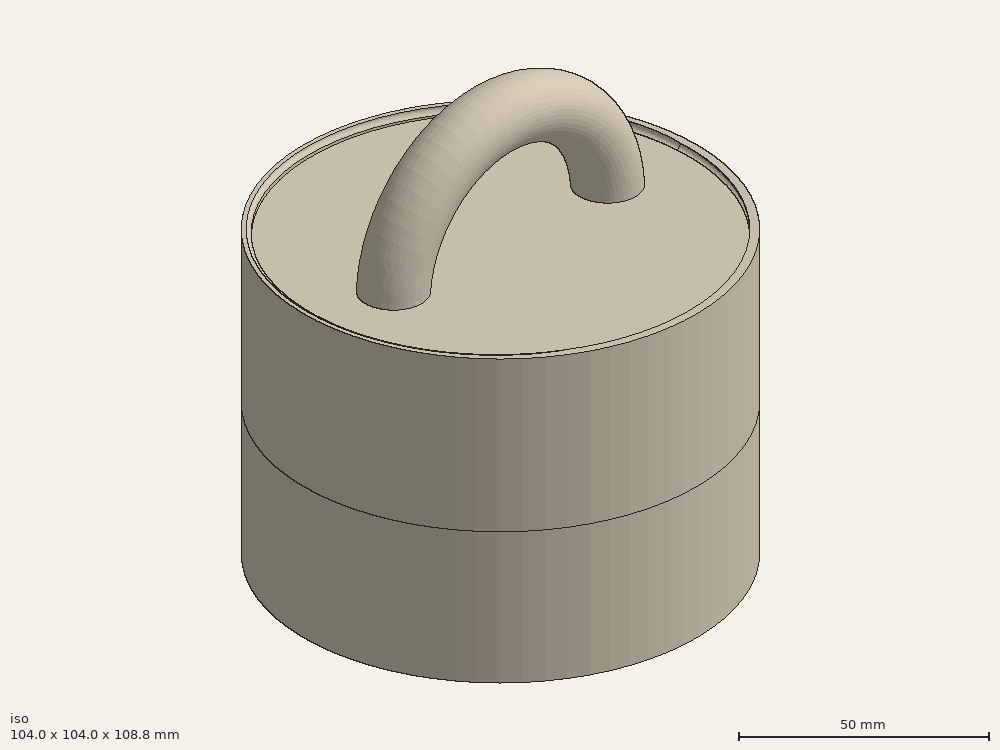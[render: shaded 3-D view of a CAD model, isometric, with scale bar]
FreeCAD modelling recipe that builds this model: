
FCSTD DOCUMENT  (FreeCAD 0.17R13522 (Git))
Label: tuna_wringer_all_3_parts
License: CreativeCommons Attribution-ShareAlike
LicenseURL: http://creativecommons.org/licenses/by-sa/4.0/
objects: Part::Cut×63, Part::Feature×46, Part::Cylinder×26, Part::MultiFuse×13, Part::Box×10, Sketcher::SketchObject×10, Part::Extrusion×9, Part::Sweep×6, PartDesign::Body×4, Part::Helix×4, Part::Ellipse×3, Part::FeaturePython×3, Part::MultiCommon×3, PartDesign::ShapeBinder×3, App::DocumentObjectGroup×3
note: 203 computed .brp shape members not serialized (recipe doc carries the construction recipe); baked Part::Feature solids carry a one-line shape summary decoded from their .brp

FEATURE [Part::Cylinder] Cylinder001  label="base_parte_inferior"
  Angle = 360
  AttacherType = Attacher::AttachEngine3D
  Height = 35
  Placement = pos=(0,0,-30) rot=(0,0,1;0rad)
  Radius = 52
FEATURE [Part::Feature] Fusion001  label="base_roscada_media_para_roscar_recipiente_inferior"
  shape: bbox 110.9 x 119.3 x 43.76 mm, 46 faces (baked)
FEATURE [Part::Cut] Cut
  Base = -> Cylinder001
  Tool = -> Fusion001
FEATURE [Part::Cylinder] Cylinder002  label="perforador_parte_inferior"
  Angle = 360
  AttacherType = Attacher::AttachEngine3D
  Height = 29
  Placement = pos=(0,0,-28) rot=(0,0,1;0rad)
  Radius = 49
FEATURE [Part::Feature] Fusion002  label="base_roscada_media001"
  shape: bbox 110.9 x 119.3 x 43.76 mm, 46 faces (baked)
FEATURE [Part::Cylinder] Cylinder003  label="Cylinder001"
  Angle = 360
  AttacherType = Attacher::AttachEngine3D
  Height = 40
  Placement = pos=(0,0,5) rot=(0,0,1;0rad)
  Radius = 52
FEATURE [Part::MultiFuse] Fusion003  label="parte_media_comienzo"
  Shapes = -> [Fusion002,Cylinder003]
FEATURE [Part::Feature] Fusion004  label="base_roscada_media002"
  Placement = pos=(0,0,8) rot=(0,0,1;0rad)
  shape: bbox 110.9 x 119.3 x 43.76 mm, 46 faces (baked)
FEATURE [Part::Cut] Cut002  label="parte_media_2"
  Base = -> Fusion003
  Tool = -> Fusion004
FEATURE [Part::Cylinder] Cylinder004  label="Cylinder002"
  Angle = 360
  AttacherType = Attacher::AttachEngine3D
  Height = 10
  Placement = pos=(0,0,-10) rot=(0,0,1;0rad)
  Radius = 60
FEATURE [Part::Cut] Cut003  label="parte_media_sin_perforar"
  Base = -> Cut002
  Tool = -> Cylinder004
FEATURE [Part::Feature] Fusion005  label="tapa_rosca"
  shape: bbox 110.9 x 119.3 x 43.76 mm, 46 faces (baked)
FEATURE [Part::Cylinder] Cylinder005  label="Cylinder003"
  Angle = 360
  AttacherType = Attacher::AttachEngine3D
  Height = 40
  Placement = pos=(0,0,4) rot=(0,0,1;0rad)
  Radius = 54
FEATURE [Part::Cut] Cut004
  Base = -> Fusion005
  Tool = -> Cylinder005
FEATURE [Part::Cylinder] Cylinder006  label="Cylinder004"
  Angle = 360
  AttacherType = Attacher::AttachEngine3D
  Height = 1
  Placement = pos=(0,0,4) rot=(0,0,1;0rad)
  Radius = 50
FEATURE [Part::MultiFuse] Fusion006
  Shapes = -> [Cut004,Cylinder006]
FEATURE [Part::Ellipse] Ellipse
  Angle0 = 0
  Angle1 = 360
  AttacherType = Attacher::AttachEngine3D
  MajorRadius = 5
  MinorRadius = 2.5
FEATURE [Part::Extrusion] Extrude
  Base = -> Ellipse
  Dir = (0,0,1)
  DirMode = 2
  FaceMakerClass = Part::FaceMakerBullseye
  LengthFwd = 20
  LengthRev = 0
  Solid = true
  Symmetric = false
FEATURE [Part::Extrusion] Extrude001
  Base = -> Ellipse
  Dir = (0,0,1)
  DirMode = 2
  FaceMakerClass = Part::FaceMakerBullseye
  LengthFwd = 20
  LengthRev = 0
  Solid = true
  Symmetric = false
FEATURE [Part::Extrusion] Extrude002
  Base = -> Ellipse
  Dir = (0,0,1)
  DirMode = 2
  FaceMakerClass = Part::FaceMakerBullseye
  LengthFwd = 20
  LengthRev = 0
  Solid = true
  Symmetric = false
FEATURE [Part::FeaturePython] Array  # Draft array (typed FeaturePython)
  Angle = 360
  ArrayType = 0
  Axis = (0,0,1)
  Base = -> Extrude
  Center = (0,0,0)
  Fuse = false
  IntervalAxis = (0,0,0)
  IntervalX = (14,0,0)
  IntervalY = (0,9,0)
  IntervalZ = (0,0,0)
  NumberPolar = 1
  NumberX = 30
  NumberY = 30
  NumberZ = 1
FEATURE [Part::Cylinder] Cylinder007  label="Cylinder005"
  Angle = 360
  AttacherType = Attacher::AttachEngine3D
  Height = 50
  Placement = pos=(77,135,-2) rot=(0,0,1;0rad)
  Radius = 48
FEATURE [Part::MultiCommon] Common
  Placement = pos=(39,-136,0) rot=(0,0,1;0rad)
  Shapes = -> [Array,Cylinder007]
FEATURE [Part::Box] Box  label="Cube"
  AttacherType = Attacher::AttachEngine3D
  Height = 60
  Length = 10
  Placement = pos=(92,40,-5) rot=(0,0,1;0rad)
  Width = 10
FEATURE [Part::Feature] Box001  label="Cube001"
  Placement = pos=(132,40,-5) rot=(0,0,1;0rad)
  shape: bbox 10 x 10 x 60 mm, 6 faces (baked)
FEATURE [Part::Feature] Box001001  label="Cube002"
  Placement = pos=(146,30,-5) rot=(0,0,1;0rad)
  shape: bbox 10 x 10 x 60 mm, 6 faces (baked)
FEATURE [Part::Feature] Box001001001  label="Cube003"
  Placement = pos=(77,30,-5) rot=(0,0,1;0rad)
  shape: bbox 10 x 10 x 60 mm, 6 faces (baked)
FEATURE [Part::Feature] Box001001001001  label="Cube004"
  Placement = pos=(77,-43,-5) rot=(0,0,1;0rad)
  shape: bbox 10 x 10 x 60 mm, 6 faces (baked)
FEATURE [Part::Feature] Box001001001001001  label="Cube005"
  Placement = pos=(146,-43,-5) rot=(0,0,1;0rad)
  shape: bbox 10 x 10 x 60 mm, 6 faces (baked)
FEATURE [Part::Feature] Box001001001001001001  label="Cube006"
  Placement = pos=(130,-52,-5) rot=(0,0,1;0rad)
  shape: bbox 10 x 10 x 60 mm, 6 faces (baked)
FEATURE [Part::Feature] Box001001001001001001001  label="Cube007"
  Placement = pos=(91,-52,-5) rot=(0,0,1;0rad)
  shape: bbox 10 x 10 x 60 mm, 6 faces (baked)
FEATURE [Part::Feature] Box001001001001001001002  label="Cube008"
  Placement = pos=(64,13,-5) rot=(0,0,1;0rad)
  shape: bbox 10 x 10 x 60 mm, 6 faces (baked)
FEATURE [Part::Feature] Box001001001001001001002001  label="Cube009"
  Placement = pos=(64,-25,-5) rot=(0,0,1;0rad)
  shape: bbox 10 x 10 x 60 mm, 6 faces (baked)
FEATURE [Part::Feature] Box001001001001001001002001001  label="Cube010"
  Placement = pos=(159,-25,-5) rot=(0,0,1;0rad)
  shape: bbox 10 x 10 x 60 mm, 6 faces (baked)
FEATURE [Part::Feature] Box001001001001001001002001001001  label="Cube011"
  Placement = pos=(159,12,-5) rot=(0,0,1;0rad)
  shape: bbox 10 x 10 x 60 mm, 6 faces (baked)
FEATURE [Part::Cut] Cut005
  Base = -> Common
  Tool = -> Box
FEATURE [Part::Cut] Cut006
  Base = -> Cut005
  Tool = -> Box001
FEATURE [Part::Cut] Cut007
  Base = -> Cut006
  Tool = -> Box001001
FEATURE [Part::Cut] Cut008
  Base = -> Cut007
  Tool = -> Box001001001
FEATURE [Part::Cut] Cut009
  Base = -> Cut008
  Tool = -> Box001001001001
FEATURE [Part::Cut] Cut010
  Base = -> Cut009
  Tool = -> Box001001001001001
FEATURE [Part::Cut] Cut011
  Base = -> Cut010
  Tool = -> Box001001001001001001
FEATURE [Part::Cut] Cut012
  Base = -> Cut011
  Tool = -> Box001001001001001001001
FEATURE [Part::Cut] Cut013
  Base = -> Cut012
  Tool = -> Box001001001001001001002
FEATURE [Part::Cut] Cut014
  Base = -> Cut013
  Tool = -> Box001001001001001001002001
FEATURE [Part::Cut] Cut015
  Base = -> Cut014
  Tool = -> Box001001001001001001002001001
FEATURE [Part::Cut] Cut016  label="rejilla"
  Base = -> Cut015
  Placement = pos=(-116,1,-9) rot=(0,0,1;0rad)
  Tool = -> Box001001001001001001002001001001
FEATURE [Part::Cut] Cut017  label="parte_media"
  Base = -> Cut003
  Tool = -> Cut016
FEATURE [Part::Box] Box001001001001001001002001001002  label="Cube012"
  AttacherType = Attacher::AttachEngine3D
  Height = 200
  Length = 200
  Placement = pos=(-89,-91,-6) rot=(0,0,1;0rad)
  Width = 200
FEATURE [Sketcher::SketchObject] Sketch001
  Placement = pos=(0,0,0) rot=(1,0,0;1.5708rad)
  sketch-geometry (1):
    g0: ArcOfCircle CenterX=0 CenterY=0 CenterZ=0 NormalX=0 NormalY=0 NormalZ=1 AngleXU=0 Radius=30.8415 StartAngle=0.00522177 EndAngle=3.12837
  constraints (1):
    c: Coincident(g0,g-1)
FEATURE [Part::Cut] Cut001  label="parte_inferior_done"
  Base = -> Cut
  Placement = pos=(0,0,-66) rot=(0,0,1;0rad)
  Tool = -> Cylinder002
FEATURE [Part::Cylinder] Cylinder
  Angle = 360
  AttacherType = Attacher::AttachEngine3D
  Height = 40
  Radius = 50
FEATURE [Sketcher::SketchObject] Sketch
  MapMode = 5
  Placement = pos=(0,0,0) rot=(1,0,0;1.5708rad)
  Support = -> [XZ_Plane]
  sketch-geometry (1):
    g0: Circle CenterX=50 CenterY=0 CenterZ=0 NormalX=0 NormalY=0 NormalZ=1 AngleXU=0 Radius=1
  constraints (3):
    c: PointOnObject(g0,g-1)
    c: Radius(g0) = 1
    c: DistanceX(g-1,g0) = 50
FEATURE [PartDesign::ShapeBinder] CopyFusion006
  Placement = pos=(0,0,4) rot=(0,0,1;0rad)
FEATURE [PartDesign::Body] Body
  Group = -> [Sketch,CopyFusion006]
  Origin = -> Origin
FEATURE [Part::Helix] Helix
  Angle = 0
  AttacherType = Attacher::AttachEngine3D
  Height = 40
  LocalCoord = 0
  Pitch = 3
  Radius = 50
  Style = 1
FEATURE [Part::Sweep] Sweep
  Frenet = false
  Sections = -> [Sketch]
  Solid = true
  Spine = -> Helix
  Transition = 1
FEATURE [Part::MultiFuse] Fusion  label="base_roscada_media"
  Shapes = -> [Sweep,Cylinder]
FEATURE [Part::Box] Box001001001001001001002001001003  label="Cube013"
  AttacherType = Attacher::AttachEngine3D
  Height = 200
  Length = 200
  Placement = pos=(-89,-91,-6) rot=(0,0,1;0rad)
  Width = 200
FEATURE [Part::Cut] Cut018
  Base = -> Cut017
  Tool = -> Box001001001001001001002001001002
FEATURE [Sketcher::SketchObject] Sketch002
  Placement = pos=(0,0,5) rot=(0,0,1;0rad)
  sketch-geometry (1):
    g0: Circle CenterX=30 CenterY=0 CenterZ=0 NormalX=0 NormalY=0 NormalZ=1 AngleXU=0 Radius=7.5
  constraints (3):
    c: PointOnObject(g0,g-1)
    c: Radius(g0) = 7.5
    c: DistanceX(g-1,g0) = 30
FEATURE [Part::Sweep] Sweep001  label="manija"
  Frenet = false
  Placement = pos=(0,0,4) rot=(0,0,1;0rad)
  Sections = -> [Sketch002]
  Solid = true
  Spine = -> Sketch001
  Transition = 1
FEATURE [Part::MultiFuse] Fusion007  label="tapa_con_rosca"
  Placement = pos=(0,0,104) rot=(0,0,1;0rad)
  Shapes = -> [Fusion006,Sweep001]
FEATURE [Part::Cut] Cut019
  Base = -> Fusion007
  Tool = -> Box001001001001001001002001001003
FEATURE [Part::Box] Box001001001001001001002001001004  label="Cube014"
  AttacherType = Attacher::AttachEngine3D
  Height = 200
  Length = 200
  Placement = pos=(-89,-91,-6) rot=(0,0,1;0rad)
  Width = 200
FEATURE [Part::Cut] Cut020
  Base = -> Fusion
  Tool = -> Box001001001001001001002001001004
FEATURE [App::DocumentObjectGroup] Group  label="not used"
  Group = -> [Body,Helix,Cut018,Cut019,Cut020,Extrude001,Extrude002,Sketch001]
FEATURE [Part::Helix] Helix001
  Angle = 0
  AttacherType = Attacher::AttachEngine3D
  Height = 40
  LocalCoord = 0
  Pitch = 3
  Radius = 50
  Style = 1
FEATURE [Sketcher::SketchObject] Sketch003
  MapMode = 5
  Placement = pos=(0,0,0) rot=(1,0,0;1.5708rad)
  Support = -> [XZ_Plane001]
  sketch-geometry (1):
    g0: Circle CenterX=49.9197 CenterY=0.004902 CenterZ=0 NormalX=0 NormalY=0 NormalZ=1 AngleXU=0 Radius=1.02
  constraints (1):
    c: Radius(g0) = 1.02
FEATURE [PartDesign::Body] Body001
  Group = -> [Sketch003]
  Origin = -> Origin001
FEATURE [Part::Cylinder] Cylinder008
  Angle = 360
  AttacherType = Attacher::AttachEngine3D
  Height = 40
  Radius = 50
FEATURE [Part::Helix] Helix002
  Angle = 0
  AttacherType = Attacher::AttachEngine3D
  Height = 40
  LocalCoord = 0
  Pitch = 3
  Radius = 50
  Style = 1
FEATURE [Sketcher::SketchObject] Sketch004
  MapMode = 5
  Placement = pos=(0,0,0) rot=(1,0,0;1.5708rad)
  Support = -> [XZ_Plane002]
  sketch-geometry (1):
    g0: Circle CenterX=50 CenterY=0 CenterZ=0 NormalX=0 NormalY=0 NormalZ=1 AngleXU=0 Radius=1
  constraints (3):
    c: PointOnObject(g0,g-1)
    c: Radius(g0) = 1
    c: DistanceX(g-1,g0) = 50
FEATURE [Part::Sweep] Sweep002
  Frenet = false
  Sections = -> [Sketch004]
  Solid = true
  Spine = -> Helix002
  Transition = 1
FEATURE [Part::MultiFuse] Fusion008  label="base_roscada_media003"
  Shapes = -> [Sweep002,Cylinder008]
FEATURE [Part::Cylinder] Cylinder009  label="base_parte_inferior001"
  Angle = 360
  AttacherType = Attacher::AttachEngine3D
  Height = 35
  Placement = pos=(0,0,-30) rot=(0,0,1;0rad)
  Radius = 52
FEATURE [Part::Feature] Fusion009  label="base_roscada_media_para_roscar_recipiente_inferior001"
  shape: bbox 110.9 x 119.3 x 43.76 mm, 46 faces (baked)
FEATURE [Part::Cut] Cut021
  Base = -> Cylinder009
  Tool = -> Fusion009
FEATURE [Part::Cylinder] Cylinder010  label="perforador_parte_inferior001"
  Angle = 360
  AttacherType = Attacher::AttachEngine3D
  Height = 29
  Placement = pos=(0,0,-28) rot=(0,0,1;0rad)
  Radius = 49
FEATURE [Part::Cut] Cut022  label="parte_inferior_done001"
  Base = -> Cut021
  Placement = pos=(0,0,-66) rot=(0,0,1;0rad)
  Tool = -> Cylinder010
FEATURE [Part::Feature] Fusion010  label="base_roscada_media004"
  shape: bbox 110.9 x 119.3 x 43.76 mm, 46 faces (baked)
FEATURE [Part::Cylinder] Cylinder011  label="Cylinder009"
  Angle = 360
  AttacherType = Attacher::AttachEngine3D
  Height = 40
  Placement = pos=(0,0,5) rot=(0,0,1;0rad)
  Radius = 52
FEATURE [Part::MultiFuse] Fusion011  label="parte_media_comienzo001"
  Shapes = -> [Fusion010,Cylinder011]
FEATURE [Part::Feature] Fusion012  label="base_roscada_media005"
  Placement = pos=(0,0,8) rot=(0,0,1;0rad)
  shape: bbox 110.9 x 119.3 x 43.76 mm, 46 faces (baked)
FEATURE [Part::Cut] Cut023  label="parte_media_003"
  Base = -> Fusion011
  Tool = -> Fusion012
FEATURE [Part::Cylinder] Cylinder012  label="Cylinder010"
  Angle = 360
  AttacherType = Attacher::AttachEngine3D
  Height = 10
  Placement = pos=(0,0,-10) rot=(0,0,1;0rad)
  Radius = 60
FEATURE [Part::Cut] Cut024  label="parte_media_sin_perforar001"
  Base = -> Cut023
  Tool = -> Cylinder012
FEATURE [Part::Feature] Fusion013  label="tapa_rosca001"
  shape: bbox 110.9 x 119.3 x 43.76 mm, 46 faces (baked)
FEATURE [Part::Cylinder] Cylinder013  label="Cylinder011"
  Angle = 360
  AttacherType = Attacher::AttachEngine3D
  Height = 40
  Placement = pos=(0,0,4) rot=(0,0,1;0rad)
  Radius = 54
FEATURE [Part::Cut] Cut025
  Base = -> Fusion013
  Tool = -> Cylinder013
FEATURE [Part::Cylinder] Cylinder014  label="Cylinder012"
  Angle = 360
  AttacherType = Attacher::AttachEngine3D
  Height = 1
  Placement = pos=(0,0,4) rot=(0,0,1;0rad)
  Radius = 50
FEATURE [Part::MultiFuse] Fusion014
  Shapes = -> [Cut025,Cylinder014]
FEATURE [PartDesign::ShapeBinder] CopyFusion007
  Placement = pos=(0,0,4) rot=(0,0,1;0rad)
FEATURE [PartDesign::Body] Body002
  Group = -> [Sketch004,CopyFusion007]
  Origin = -> Origin002
FEATURE [Sketcher::SketchObject] Sketch005
  Placement = pos=(0,0,0) rot=(1,0,0;1.5708rad)
  sketch-geometry (1):
    g0: ArcOfCircle CenterX=0 CenterY=0 CenterZ=0 NormalX=0 NormalY=0 NormalZ=1 AngleXU=0 Radius=30.8415 StartAngle=0.00522177 EndAngle=3.12837
  constraints (1):
    c: Coincident(g0,g-1)
FEATURE [Sketcher::SketchObject] Sketch006
  Placement = pos=(0,0,5) rot=(0,0,1;0rad)
  sketch-geometry (1):
    g0: Circle CenterX=30 CenterY=0 CenterZ=0 NormalX=0 NormalY=0 NormalZ=1 AngleXU=0 Radius=7.5
  constraints (3):
    c: PointOnObject(g0,g-1)
    c: Radius(g0) = 7.5
    c: DistanceX(g-1,g0) = 30
FEATURE [Part::Sweep] Sweep003  label="manija001"
  Frenet = false
  Placement = pos=(0,0,4) rot=(0,0,1;0rad)
  Sections = -> [Sketch006]
  Solid = true
  Spine = -> Sketch005
  Transition = 1
FEATURE [Part::MultiFuse] Fusion015  label="tapa_con_rosca001"
  Placement = pos=(0,0,104) rot=(0,0,1;0rad)
  Shapes = -> [Fusion014,Sweep003]
FEATURE [Part::Ellipse] Ellipse001
  Angle0 = 0
  Angle1 = 360
  AttacherType = Attacher::AttachEngine3D
  MajorRadius = 5
  MinorRadius = 2.5
FEATURE [Part::Extrusion] Extrude003
  Base = -> Ellipse001
  Dir = (0,0,1)
  DirMode = 2
  FaceMakerClass = Part::FaceMakerBullseye
  LengthFwd = 20
  LengthRev = 0
  Solid = true
  Symmetric = false
FEATURE [Part::Extrusion] Extrude004
  Base = -> Ellipse001
  Dir = (0,0,1)
  DirMode = 2
  FaceMakerClass = Part::FaceMakerBullseye
  LengthFwd = 20
  LengthRev = 0
  Solid = true
  Symmetric = false
FEATURE [Part::Extrusion] Extrude005
  Base = -> Ellipse001
  Dir = (0,0,1)
  DirMode = 2
  FaceMakerClass = Part::FaceMakerBullseye
  LengthFwd = 20
  LengthRev = 0
  Solid = true
  Symmetric = false
FEATURE [Part::FeaturePython] Array001  # Draft array (typed FeaturePython)
  Angle = 360
  ArrayType = 0
  Axis = (0,0,1)
  Base = -> Extrude003
  Center = (0,0,0)
  Fuse = false
  IntervalAxis = (0,0,0)
  IntervalX = (14,0,0)
  IntervalY = (0,9,0)
  IntervalZ = (0,0,0)
  NumberPolar = 1
  NumberX = 30
  NumberY = 30
  NumberZ = 1
FEATURE [Part::Cylinder] Cylinder015  label="Cylinder013"
  Angle = 360
  AttacherType = Attacher::AttachEngine3D
  Height = 50
  Placement = pos=(77,135,-2) rot=(0,0,1;0rad)
  Radius = 48
FEATURE [Part::MultiCommon] Common001
  Placement = pos=(39,-136,0) rot=(0,0,1;0rad)
  Shapes = -> [Array001,Cylinder015]
FEATURE [Part::Box] Box001001001001001001002001001005  label="Cube015"
  AttacherType = Attacher::AttachEngine3D
  Height = 60
  Length = 10
  Placement = pos=(92,40,-5) rot=(0,0,1;0rad)
  Width = 10
FEATURE [Part::Feature] Box001001001001001001002001001006  label="Cube016"
  Placement = pos=(132,40,-5) rot=(0,0,1;0rad)
  shape: bbox 10 x 10 x 60 mm, 6 faces (baked)
FEATURE [Part::Feature] Box001001001001001001002001001007  label="Cube017"
  Placement = pos=(146,30,-5) rot=(0,0,1;0rad)
  shape: bbox 10 x 10 x 60 mm, 6 faces (baked)
FEATURE [Part::Feature] Box001001001001001001002001001008  label="Cube018"
  Placement = pos=(77,30,-5) rot=(0,0,1;0rad)
  shape: bbox 10 x 10 x 60 mm, 6 faces (baked)
FEATURE [Part::Feature] Box001001001001001001002001001009  label="Cube019"
  Placement = pos=(77,-43,-5) rot=(0,0,1;0rad)
  shape: bbox 10 x 10 x 60 mm, 6 faces (baked)
FEATURE [Part::Feature] Box001001001001001001002001001010  label="Cube020"
  Placement = pos=(146,-43,-5) rot=(0,0,1;0rad)
  shape: bbox 10 x 10 x 60 mm, 6 faces (baked)
FEATURE [Part::Feature] Box001001001001001001002001001011  label="Cube021"
  Placement = pos=(130,-52,-5) rot=(0,0,1;0rad)
  shape: bbox 10 x 10 x 60 mm, 6 faces (baked)
FEATURE [Part::Feature] Box001001001001001001002001001012  label="Cube022"
  Placement = pos=(91,-52,-5) rot=(0,0,1;0rad)
  shape: bbox 10 x 10 x 60 mm, 6 faces (baked)
FEATURE [Part::Feature] Box001001001001001001002001001013  label="Cube023"
  Placement = pos=(64,13,-5) rot=(0,0,1;0rad)
  shape: bbox 10 x 10 x 60 mm, 6 faces (baked)
FEATURE [Part::Feature] Box001001001001001001002001001014  label="Cube024"
  Placement = pos=(64,-25,-5) rot=(0,0,1;0rad)
  shape: bbox 10 x 10 x 60 mm, 6 faces (baked)
FEATURE [Part::Feature] Box001001001001001001002001001015  label="Cube025"
  Placement = pos=(159,-25,-5) rot=(0,0,1;0rad)
  shape: bbox 10 x 10 x 60 mm, 6 faces (baked)
FEATURE [Part::Feature] Box001001001001001001002001001016  label="Cube026"
  Placement = pos=(159,12,-5) rot=(0,0,1;0rad)
  shape: bbox 10 x 10 x 60 mm, 6 faces (baked)
FEATURE [Part::Cut] Cut026
  Base = -> Common001
  Tool = -> Box001001001001001001002001001005
FEATURE [Part::Cut] Cut027
  Base = -> Cut026
  Tool = -> Box001001001001001001002001001006
FEATURE [Part::Cut] Cut028
  Base = -> Cut027
  Tool = -> Box001001001001001001002001001007
FEATURE [Part::Cut] Cut029
  Base = -> Cut028
  Tool = -> Box001001001001001001002001001008
FEATURE [Part::Cut] Cut030
  Base = -> Cut029
  Tool = -> Box001001001001001001002001001009
FEATURE [Part::Cut] Cut031
  Base = -> Cut030
  Tool = -> Box001001001001001001002001001010
FEATURE [Part::Cut] Cut032
  Base = -> Cut031
  Tool = -> Box001001001001001001002001001011
FEATURE [Part::Cut] Cut033
  Base = -> Cut032
  Tool = -> Box001001001001001001002001001012
FEATURE [Part::Cut] Cut034
  Base = -> Cut033
  Tool = -> Box001001001001001001002001001013
FEATURE [Part::Cut] Cut035
  Base = -> Cut034
  Tool = -> Box001001001001001001002001001014
FEATURE [Part::Cut] Cut036
  Base = -> Cut035
  Tool = -> Box001001001001001001002001001015
FEATURE [Part::Cut] Cut037  label="rejilla001"
  Base = -> Cut036
  Placement = pos=(-116,1,-9) rot=(0,0,1;0rad)
  Tool = -> Box001001001001001001002001001016
FEATURE [Part::Cut] Cut038  label="parte_media001"
  Base = -> Cut024
  Placement = pos=(0,0,-66) rot=(0,0,1;0rad)
  Tool = -> Cut037
FEATURE [Part::Box] Box001001001001001001002001001017  label="Cube027"
  AttacherType = Attacher::AttachEngine3D
  Height = 100
  Length = 120
  Placement = pos=(-60,-60,61) rot=(0,0,1;0rad)
  Width = 120
FEATURE [Part::Box] Box001001001001001001002001001018  label="Cube028"
  AttacherType = Attacher::AttachEngine3D
  Height = 100
  Length = 120
  Placement = pos=(-60,-60,-120) rot=(0,0,1;0rad)
  Width = 120
FEATURE [Part::Cut] Cut039
  Base = -> Fusion015
  Tool = -> Box001001001001001001002001001017
FEATURE [Part::Cut] Cut040
  Base = -> Cut022
  Tool = -> Box001001001001001001002001001018
FEATURE [App::DocumentObjectGroup] Group001  label="not used001"
  Group = -> [Cut040,Cut039,Helix002,Body002,Fusion008,Sketch005,Extrude004,Extrude005]
FEATURE [Part::Cylinder] Cylinder016
  Angle = 360
  AttacherType = Attacher::AttachEngine3D
  Height = 40
  Radius = 50
FEATURE [Part::Helix] Helix003
  Angle = 0
  AttacherType = Attacher::AttachEngine3D
  Height = 40
  LocalCoord = 0
  Pitch = 3
  Radius = 50
  Style = 1
FEATURE [Sketcher::SketchObject] Sketch007
  MapMode = 5
  Placement = pos=(0,0,0) rot=(1,0,0;1.5708rad)
  Support = -> [XZ_Plane003]
  sketch-geometry (1):
    g0: Circle CenterX=50 CenterY=0 CenterZ=0 NormalX=0 NormalY=0 NormalZ=1 AngleXU=0 Radius=1
  constraints (3):
    c: PointOnObject(g0,g-1)
    c: Radius(g0) = 1
    c: DistanceX(g-1,g0) = 50
FEATURE [Part::Sweep] Sweep004
  Frenet = false
  Sections = -> [Sketch007]
  Solid = true
  Spine = -> Helix003
  Transition = 1
FEATURE [Part::MultiFuse] Fusion016  label="base_roscada_media006"
  Shapes = -> [Sweep004,Cylinder016]
FEATURE [Part::Cylinder] Cylinder017  label="base_parte_inferior002"
  Angle = 360
  AttacherType = Attacher::AttachEngine3D
  Height = 35
  Placement = pos=(0,0,-30) rot=(0,0,1;0rad)
  Radius = 52
FEATURE [Part::Feature] Fusion017  label="base_roscada_media_para_roscar_recipiente_inferior002"
  shape: bbox 110.9 x 119.3 x 43.76 mm, 46 faces (baked)
FEATURE [Part::Cut] Cut041
  Base = -> Cylinder017
  Tool = -> Fusion017
FEATURE [Part::Cylinder] Cylinder018  label="perforador_parte_inferior002"
  Angle = 360
  AttacherType = Attacher::AttachEngine3D
  Height = 29
  Placement = pos=(0,0,-28) rot=(0,0,1;0rad)
  Radius = 49
FEATURE [Part::Cut] Cut042  label="parte_inferior_done002"
  Base = -> Cut041
  Placement = pos=(0,0,-66) rot=(0,0,1;0rad)
  Tool = -> Cylinder018
FEATURE [Part::Feature] Fusion018  label="base_roscada_media007"
  shape: bbox 110.9 x 119.3 x 43.76 mm, 46 faces (baked)
FEATURE [Part::Cylinder] Cylinder019  label="Cylinder017"
  Angle = 360
  AttacherType = Attacher::AttachEngine3D
  Height = 40
  Placement = pos=(0,0,5) rot=(0,0,1;0rad)
  Radius = 52
FEATURE [Part::MultiFuse] Fusion019  label="parte_media_comienzo002"
  Shapes = -> [Fusion018,Cylinder019]
FEATURE [Part::Feature] Fusion020  label="base_roscada_media008"
  Placement = pos=(0,0,8) rot=(0,0,1;0rad)
  shape: bbox 110.9 x 119.3 x 43.76 mm, 46 faces (baked)
FEATURE [Part::Cut] Cut043  label="parte_media_004"
  Base = -> Fusion019
  Tool = -> Fusion020
FEATURE [Part::Cylinder] Cylinder020  label="Cylinder018"
  Angle = 360
  AttacherType = Attacher::AttachEngine3D
  Height = 10
  Placement = pos=(0,0,-10) rot=(0,0,1;0rad)
  Radius = 60
FEATURE [Part::Cut] Cut044  label="parte_media_sin_perforar002"
  Base = -> Cut043
  Tool = -> Cylinder020
FEATURE [Part::Feature] Fusion021  label="tapa_rosca002"
  shape: bbox 110.9 x 119.3 x 43.76 mm, 46 faces (baked)
FEATURE [Part::Cylinder] Cylinder021  label="Cylinder019"
  Angle = 360
  AttacherType = Attacher::AttachEngine3D
  Height = 40
  Placement = pos=(0,0,4) rot=(0,0,1;0rad)
  Radius = 54
FEATURE [Part::Cut] Cut045
  Base = -> Fusion021
  Tool = -> Cylinder021
FEATURE [Part::Cylinder] Cylinder022  label="Cylinder020"
  Angle = 360
  AttacherType = Attacher::AttachEngine3D
  Height = 1
  Placement = pos=(0,0,4) rot=(0,0,1;0rad)
  Radius = 50
FEATURE [Part::MultiFuse] Fusion022
  Shapes = -> [Cut045,Cylinder022]
FEATURE [PartDesign::ShapeBinder] CopyFusion008
  Placement = pos=(0,0,4) rot=(0,0,1;0rad)
FEATURE [PartDesign::Body] Body003
  Group = -> [Sketch007,CopyFusion008]
  Origin = -> Origin003
FEATURE [Sketcher::SketchObject] Sketch008
  Placement = pos=(0,0,0) rot=(1,0,0;1.5708rad)
  sketch-geometry (1):
    g0: ArcOfCircle CenterX=0 CenterY=0 CenterZ=0 NormalX=0 NormalY=0 NormalZ=1 AngleXU=0 Radius=30.8415 StartAngle=0.00522177 EndAngle=3.12837
  constraints (1):
    c: Coincident(g0,g-1)
FEATURE [Sketcher::SketchObject] Sketch009
  Placement = pos=(0,0,5) rot=(0,0,1;0rad)
  sketch-geometry (1):
    g0: Circle CenterX=30 CenterY=0 CenterZ=0 NormalX=0 NormalY=0 NormalZ=1 AngleXU=0 Radius=7.5
  constraints (3):
    c: PointOnObject(g0,g-1)
    c: Radius(g0) = 7.5
    c: DistanceX(g-1,g0) = 30
FEATURE [Part::Sweep] Sweep005  label="manija002"
  Frenet = false
  Placement = pos=(0,0,3) rot=(0,0,1;0rad)
  Sections = -> [Sketch009]
  Solid = true
  Spine = -> Sketch008
  Transition = 1
FEATURE [Part::MultiFuse] Fusion023  label="tapa_con_rosca002"
  Placement = pos=(0,0,104) rot=(0,0,1;0rad)
  Shapes = -> [Fusion022,Sweep005]
FEATURE [Part::Ellipse] Ellipse002
  Angle0 = 0
  Angle1 = 360
  AttacherType = Attacher::AttachEngine3D
  MajorRadius = 5
  MinorRadius = 2.5
FEATURE [Part::Extrusion] Extrude006
  Base = -> Ellipse002
  Dir = (0,0,1)
  DirMode = 2
  FaceMakerClass = Part::FaceMakerBullseye
  LengthFwd = 20
  LengthRev = 0
  Solid = true
  Symmetric = false
FEATURE [Part::Extrusion] Extrude007
  Base = -> Ellipse002
  Dir = (0,0,1)
  DirMode = 2
  FaceMakerClass = Part::FaceMakerBullseye
  LengthFwd = 20
  LengthRev = 0
  Solid = true
  Symmetric = false
FEATURE [Part::Extrusion] Extrude008
  Base = -> Ellipse002
  Dir = (0,0,1)
  DirMode = 2
  FaceMakerClass = Part::FaceMakerBullseye
  LengthFwd = 20
  LengthRev = 0
  Solid = true
  Symmetric = false
FEATURE [Part::FeaturePython] Array002  # Draft array (typed FeaturePython)
  Angle = 360
  ArrayType = 0
  Axis = (0,0,1)
  Base = -> Extrude006
  Center = (0,0,0)
  Fuse = false
  IntervalAxis = (0,0,0)
  IntervalX = (14,0,0)
  IntervalY = (0,9,0)
  IntervalZ = (0,0,0)
  NumberPolar = 1
  NumberX = 30
  NumberY = 30
  NumberZ = 1
FEATURE [Part::Cylinder] Cylinder023  label="Cylinder021"
  Angle = 360
  AttacherType = Attacher::AttachEngine3D
  Height = 50
  Placement = pos=(77,135,-2) rot=(0,0,1;0rad)
  Radius = 48
FEATURE [Part::MultiCommon] Common002
  Placement = pos=(39,-136,0) rot=(0,0,1;0rad)
  Shapes = -> [Array002,Cylinder023]
FEATURE [Part::Box] Box001001001001001001002001001019  label="Cube029"
  AttacherType = Attacher::AttachEngine3D
  Height = 60
  Length = 10
  Placement = pos=(92,40,-5) rot=(0,0,1;0rad)
  Width = 10
FEATURE [Part::Feature] Box001001001001001001002001001020  label="Cube030"
  Placement = pos=(132,40,-5) rot=(0,0,1;0rad)
  shape: bbox 10 x 10 x 60 mm, 6 faces (baked)
FEATURE [Part::Feature] Box001001001001001001002001001021  label="Cube031"
  Placement = pos=(146,30,-5) rot=(0,0,1;0rad)
  shape: bbox 10 x 10 x 60 mm, 6 faces (baked)
FEATURE [Part::Feature] Box001001001001001001002001001022  label="Cube032"
  Placement = pos=(77,30,-5) rot=(0,0,1;0rad)
  shape: bbox 10 x 10 x 60 mm, 6 faces (baked)
FEATURE [Part::Feature] Box001001001001001001002001001023  label="Cube033"
  Placement = pos=(77,-43,-5) rot=(0,0,1;0rad)
  shape: bbox 10 x 10 x 60 mm, 6 faces (baked)
FEATURE [Part::Feature] Box001001001001001001002001001024  label="Cube034"
  Placement = pos=(146,-43,-5) rot=(0,0,1;0rad)
  shape: bbox 10 x 10 x 60 mm, 6 faces (baked)
FEATURE [Part::Feature] Box001001001001001001002001001025  label="Cube035"
  Placement = pos=(130,-52,-5) rot=(0,0,1;0rad)
  shape: bbox 10 x 10 x 60 mm, 6 faces (baked)
FEATURE [Part::Feature] Box001001001001001001002001001026  label="Cube036"
  Placement = pos=(91,-52,-5) rot=(0,0,1;0rad)
  shape: bbox 10 x 10 x 60 mm, 6 faces (baked)
FEATURE [Part::Feature] Box001001001001001001002001001027  label="Cube037"
  Placement = pos=(64,13,-5) rot=(0,0,1;0rad)
  shape: bbox 10 x 10 x 60 mm, 6 faces (baked)
FEATURE [Part::Feature] Box001001001001001001002001001028  label="Cube038"
  Placement = pos=(64,-25,-5) rot=(0,0,1;0rad)
  shape: bbox 10 x 10 x 60 mm, 6 faces (baked)
FEATURE [Part::Feature] Box001001001001001001002001001029  label="Cube039"
  Placement = pos=(159,-25,-5) rot=(0,0,1;0rad)
  shape: bbox 10 x 10 x 60 mm, 6 faces (baked)
FEATURE [Part::Feature] Box001001001001001001002001001030  label="Cube040"
  Placement = pos=(159,12,-5) rot=(0,0,1;0rad)
  shape: bbox 10 x 10 x 60 mm, 6 faces (baked)
FEATURE [Part::Cut] Cut046
  Base = -> Common002
  Tool = -> Box001001001001001001002001001019
FEATURE [Part::Cut] Cut047
  Base = -> Cut046
  Tool = -> Box001001001001001001002001001020
FEATURE [Part::Cut] Cut048
  Base = -> Cut047
  Tool = -> Box001001001001001001002001001021
FEATURE [Part::Cut] Cut049
  Base = -> Cut048
  Tool = -> Box001001001001001001002001001022
FEATURE [Part::Cut] Cut050
  Base = -> Cut049
  Tool = -> Box001001001001001001002001001023
FEATURE [Part::Cut] Cut051
  Base = -> Cut050
  Tool = -> Box001001001001001001002001001024
FEATURE [Part::Cut] Cut052
  Base = -> Cut051
  Tool = -> Box001001001001001001002001001025
FEATURE [Part::Cut] Cut053
  Base = -> Cut052
  Tool = -> Box001001001001001001002001001026
FEATURE [Part::Cut] Cut054
  Base = -> Cut053
  Tool = -> Box001001001001001001002001001027
FEATURE [Part::Cut] Cut055
  Base = -> Cut054
  Tool = -> Box001001001001001001002001001028
FEATURE [Part::Cut] Cut056
  Base = -> Cut055
  Tool = -> Box001001001001001001002001001029
FEATURE [Part::Cut] Cut057  label="rejilla002"
  Base = -> Cut056
  Placement = pos=(-116,1,-9) rot=(0,0,1;0rad)
  Tool = -> Box001001001001001001002001001030
FEATURE [Part::Cut] Cut058  label="parte_media002"
  Base = -> Cut044
  Tool = -> Cut057
FEATURE [Part::Box] Box001001001001001001002001001031  label="Cube041"
  AttacherType = Attacher::AttachEngine3D
  Height = 165
  Length = 120
  Placement = pos=(-60,-58,-112) rot=(0,0,1;0rad)
  Width = 120
FEATURE [Part::Box] Box001001001001001001002001001032  label="Cube042"
  AttacherType = Attacher::AttachEngine3D
  Height = 165
  Length = 120
  Placement = pos=(-60,-58,-112) rot=(0,0,1;0rad)
  Width = 120
FEATURE [Part::Cut] Cut059
  Base = -> Cut058
  Tool = -> Box001001001001001001002001001031
FEATURE [Part::Cut] Cut060
  Base = -> Cut042
  Tool = -> Box001001001001001001002001001032
FEATURE [App::DocumentObjectGroup] Group002  label="not used002"
  Group = -> [Extrude007,Extrude008,Cut059,Cut060,Helix003,Body003,Fusion016,Sketch008]
FEATURE [Part::Cylinder] Cylinder024  label="Cylinder022"
  Angle = 360
  AttacherType = Attacher::AttachEngine3D
  Height = 10
  Placement = pos=(0,0,98) rot=(0,0,1;0rad)
  Radius = 60
FEATURE [Part::Cut] Cut061  label="tapa_sin_rosca"
  Base = -> Fusion023
  Tool = -> Cylinder024
FEATURE [Part::Feature] Cut022001  label="Cut023"
  Placement = pos=(0,0,-55) rot=(0,0,1;0rad)
  shape: bbox 108.9 x 117.3 x 43.86 mm, 42 faces (baked)
FEATURE [Part::Cylinder] Cylinder025  label="Cylinder023"
  Angle = 360
  AttacherType = Attacher::AttachEngine3D
  Height = 50
  Placement = pos=(0,0,-45) rot=(0,0,1;0rad)
  Radius = 60
FEATURE [Part::Cut] Cut022002
  Base = -> Cut022001
  Placement = pos=(0,0,153) rot=(0,0,1;0rad)
  Tool = -> Cylinder025
FEATURE [Part::MultiFuse] Fusion024  label="tapa_con_rosca_098"
  Placement = pos=(0,0,-132) rot=(0,0,1;0rad)
  Shapes = -> [Cut061,Cut022002]
